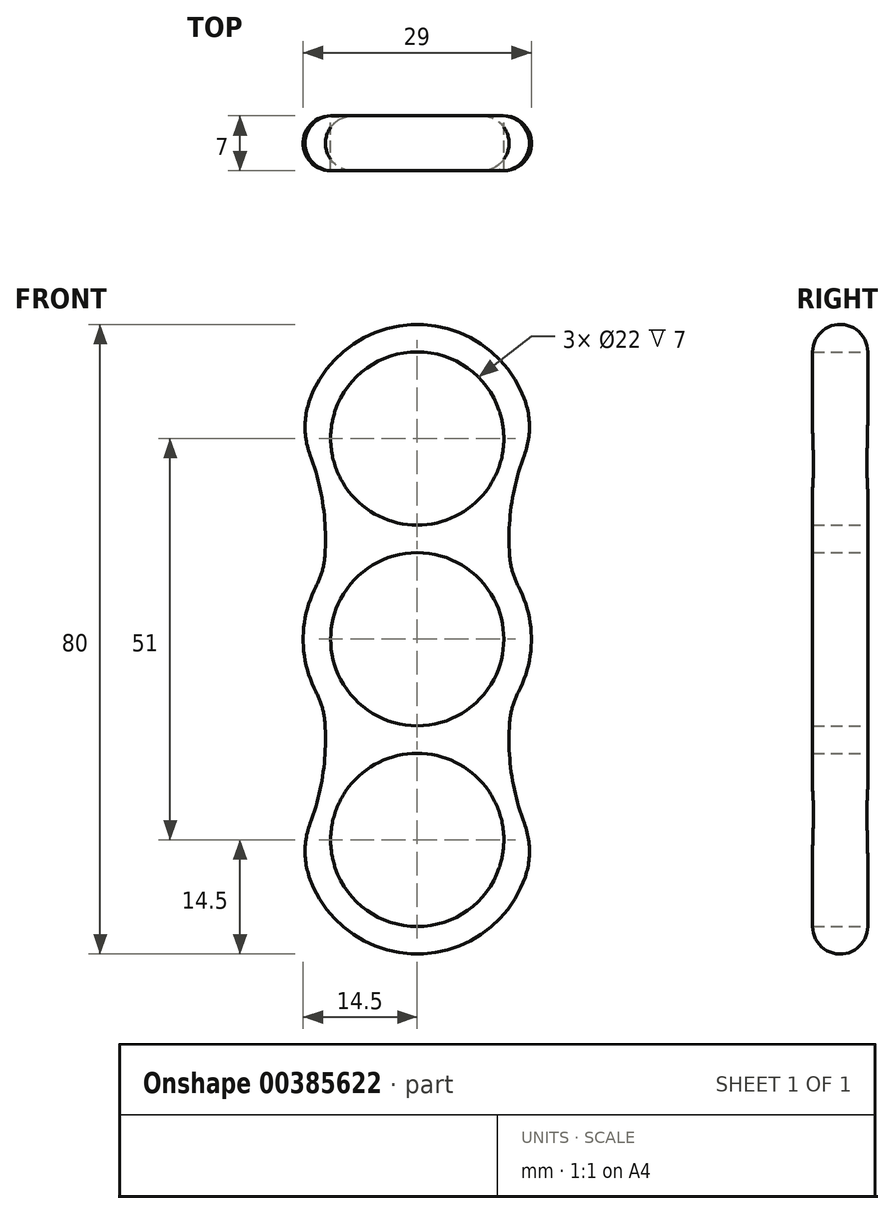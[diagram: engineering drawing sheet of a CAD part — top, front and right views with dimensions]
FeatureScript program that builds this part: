
annotation { "Feature Type Name" : "Feature", "Feature Type Description" : "" }
export const myFeature = defineFeature(function(context is Context, id is Id, definition is map)
    precondition{}
    {
        {
            var Q0;
            Q0=qCreatedBy(makeId("Front.planeOp"),FACE);
            var sketch = newSketch(context, id + "F0", { "sketchPlane" : qUnion([Q0])});
            skCircle(sketch, "E0", {"center": v(0, 0) * mm, "radius": 11 * mm});
            skCircle(sketch, "E1", {"center": v(0, 25.5) * mm, "radius": 11 * mm});
            skArc(sketch, "E2", {"start": v(-12.85, 6.73) * mm, "mid": v(-14.5, 0) * mm, "end": v(-12.85, -6.73) * mm});
            skArc(sketch, "E3.converted", {"start": v(13.73, 30.17) * mm, "mid": v(0, 40) * mm, "end": v(-13.73, 30.17) * mm});
            skCircle(sketch, "E4.1.0", {"center": v(0, -25.5) * mm, "radius": 11 * mm});
            skArc(sketch, "E4.1.1", {"start": v(-13.73, -30.17) * mm, "mid": v(0, -40) * mm, "end": v(13.73, -30.17) * mm});
            skArc(sketch, "E5", {"start": v(-11.73, 10.67) * mm, "mid": v(-11.98, 17.14) * mm, "end": v(-13.6, 23.4) * mm});
            skArc(sketch, "E6", {"start": v(-13.6, -23.4) * mm, "mid": v(-11.98, -17.14) * mm, "end": v(-11.73, -10.67) * mm});
            skArc(sketch, "E7", {"start": v(11.73, -10.67) * mm, "mid": v(11.98, -17.14) * mm, "end": v(13.6, -23.4) * mm});
            skArc(sketch, "E8", {"start": v(13.6, 23.4) * mm, "mid": v(11.98, 17.14) * mm, "end": v(11.73, 10.67) * mm});
            skPoint(sketch, "E9", {"position": v(6.9, 12.75) * mm});
            skPoint(sketch, "E10", {"position": v(-6.9, 12.75) * mm});
            skPoint(sketch, "E11", {"position": v(6.9, -12.75) * mm});
            skPoint(sketch, "E12", {"position": v(-6.9, -12.75) * mm});
            skPoint(sketch, "E13.orphan", {"position": v(-14.5, 0) * mm});
            skArc(sketch, "E14.trimOffspring", {"start": v(12.85, -6.73) * mm, "mid": v(14.5, 0) * mm, "end": v(12.85, 6.73) * mm});
            skPoint(sketch, "E15.orphan", {"position": v(14.5, 0) * mm});
            skPoint(sketch, "E16.visualSharp", {"position": v(-12.02, 8.12) * mm});
            skArc(sketch, "E16.filletArc", {"start": v(-12.85, 6.73) * mm, "mid": v(-12.08, 8.64) * mm, "end": v(-11.73, 10.67) * mm});
            skPoint(sketch, "E17.visualSharp", {"position": v(-14.5, 25.5) * mm});
            skArc(sketch, "E17.filletArc", {"start": v(-13.73, 30.17) * mm, "mid": v(-14.26, 26.77) * mm, "end": v(-13.6, 23.4) * mm});
            skPoint(sketch, "E18.visualSharp", {"position": v(14.5, 25.5) * mm});
            skArc(sketch, "E18.filletArc", {"start": v(13.6, 23.4) * mm, "mid": v(14.26, 26.77) * mm, "end": v(13.73, 30.17) * mm});
            skPoint(sketch, "E19.visualSharp", {"position": v(12.02, 8.12) * mm});
            skArc(sketch, "E19.filletArc", {"start": v(11.73, 10.67) * mm, "mid": v(12.08, 8.64) * mm, "end": v(12.85, 6.73) * mm});
            skPoint(sketch, "E20.visualSharp", {"position": v(12.02, -8.12) * mm});
            skArc(sketch, "E20.filletArc", {"start": v(12.85, -6.73) * mm, "mid": v(12.08, -8.64) * mm, "end": v(11.73, -10.67) * mm});
            skPoint(sketch, "E21.visualSharp", {"position": v(-12.02, -8.12) * mm});
            skArc(sketch, "E21.filletArc", {"start": v(-11.73, -10.67) * mm, "mid": v(-12.08, -8.64) * mm, "end": v(-12.85, -6.73) * mm});
            skPoint(sketch, "E22.visualSharp", {"position": v(-14.5, -25.5) * mm});
            skArc(sketch, "E22.filletArc", {"start": v(-13.6, -23.4) * mm, "mid": v(-14.26, -26.77) * mm, "end": v(-13.73, -30.17) * mm});
            skPoint(sketch, "E23.visualSharp", {"position": v(14.5, -25.5) * mm});
            skArc(sketch, "E23.filletArc", {"start": v(13.73, -30.17) * mm, "mid": v(14.26, -26.77) * mm, "end": v(13.6, -23.4) * mm});
            skSolve(sketch);
        }
        {
            var Q0;
            Q0=makeQuery(id+"F0.imprint","IMPRINT",FACE,{"disambiguationData":[TD([[makeQuery(id+"F0.imprint","IMPRINT",EDGE,{"derivedFrom":sQuery(id+"F0.wireOp",EDGE,"E0")}),-1.0]])]});
            extrude(context, id + "F1", {"entities" : qUnion([Q0]), "depth" : 7 * mm, "offsetDistance" : 25 * mm});
        }
        {
            var Q0;
            Q0=makeQuery(id+"F1.opExtrude","CAP_EDGE",EDGE,{"disambiguationData":[OSD([sQuery(id+"F0.wireOp",EDGE,"E3.converted")])],"isStart":false});
            var Q1;
            Q1=makeQuery(id+"F1.opExtrude","CAP_EDGE",EDGE,{"disambiguationData":[OSD([sQuery(id+"F0.wireOp",EDGE,"E3.converted")])],"isStart":true});
            fillet(context, id + "F2", {"entities" : qUnion([Q0, Q1]), "radius" : 3.5 * mm, "tangentPropagation" : true, "allowEdgeOverflow" : false});
        }
    });
